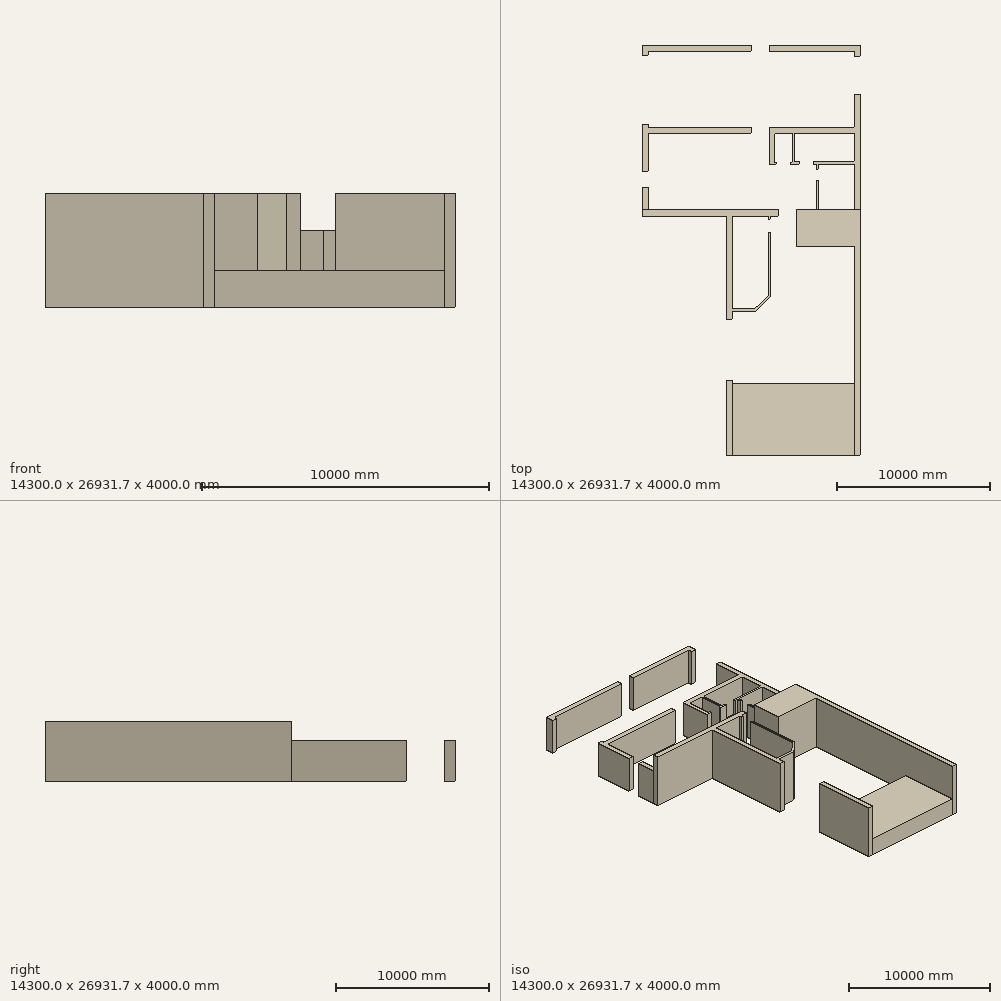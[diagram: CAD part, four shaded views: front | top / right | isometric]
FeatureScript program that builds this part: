
annotation { "Feature Type Name" : "Feature", "Feature Type Description" : "" }
export const myFeature = defineFeature(function(context is Context, id is Id, definition is map)
    precondition{}
    {
        {
            var Q0;
            Q0=qCreatedBy(makeId("Top.planeOp"),FACE);
            var sketch = newSketch(context, id + "F0", { "sketchPlane" : qUnion([Q0])});
            skLineSegment(sketch, "E0.bottom", {"start": v(-6984.38, 2004.34) * mm, "end": v(-234.38, 2004.34) * mm});
            skLineSegment(sketch, "E0.top", {"start": v(-6984.38, -2995.66) * mm, "end": v(-234.38, -2995.66) * mm});
            skLineSegment(sketch, "E0.left", {"start": v(-6984.38, 2004.34) * mm, "end": v(-6984.38, 1751.04) * mm});
            skLineSegment(sketch, "E0.right", {"start": v(6515.62, 2004.34) * mm, "end": v(6515.62, 1701.04) * mm});
            skLineSegment(sketch, "E1.0", {"start": v(-7384.38, 2404.34) * mm, "end": v(-234.38, 2404.34) * mm});
            skLineSegment(sketch, "E1.1", {"start": v(-7384.38, 2404.34) * mm, "end": v(-7384.38, 1751.04) * mm});
            skLineSegment(sketch, "E1.2", {"start": v(-7384.38, -3395.66) * mm, "end": v(-234.38, -3395.66) * mm});
            skLineSegment(sketch, "E1.3", {"start": v(6915.62, 2404.34) * mm, "end": v(6915.62, 1701.04) * mm});
            skLineSegment(sketch, "E2", {"start": v(-234.38, -3395.66) * mm, "end": v(-234.38, -2995.66) * mm});
            skLineSegment(sketch, "E3", {"start": v(965.62, -2995.66) * mm, "end": v(965.62, -3395.66) * mm});
            skLineSegment(sketch, "E4.trimOffspring", {"start": v(965.62, -2995.66) * mm, "end": v(6515.62, -2995.66) * mm});
            skLineSegment(sketch, "E5.trimOffspring", {"start": v(2615.62, -3395.66) * mm, "end": v(6515.62, -3395.66) * mm});
            skLineSegment(sketch, "E6", {"start": v(6515.62, 1701.04) * mm, "end": v(6915.62, 1701.04) * mm});
            skLineSegment(sketch, "E7", {"start": v(6515.62, -798.96) * mm, "end": v(6915.62, -798.96) * mm});
            skLineSegment(sketch, "E8", {"start": v(965.62, 2004.34) * mm, "end": v(965.62, 2404.34) * mm});
            skLineSegment(sketch, "E9", {"start": v(-234.38, 2004.34) * mm, "end": v(-234.38, 2404.34) * mm});
            skPoint(sketch, "E9.endSnap0", {"position": v(-234.38, 2004.34) * mm});
            skLineSegment(sketch, "E10.trimOffspring", {"start": v(965.62, 2404.34) * mm, "end": v(6915.62, 2404.34) * mm});
            skLineSegment(sketch, "E11.trimOffspring", {"start": v(965.62, 2004.34) * mm, "end": v(6515.62, 2004.34) * mm});
            skLineSegment(sketch, "E12.trimOffspring", {"start": v(6515.62, -798.96) * mm, "end": v(6515.62, -2995.66) * mm});
            skLineSegment(sketch, "E13.trimOffspring", {"start": v(6915.62, -798.96) * mm, "end": v(6915.62, -3395.66) * mm});
            skLineSegment(sketch, "E14", {"start": v(-6984.38, 1751.04) * mm, "end": v(-7384.38, 1751.04) * mm});
            skLineSegment(sketch, "E15", {"start": v(-6984.38, -2795.46) * mm, "end": v(-7384.38, -2795.46) * mm});
            skLineSegment(sketch, "E16.trimOffspring", {"start": v(-6984.38, -2795.46) * mm, "end": v(-6984.38, -2995.66) * mm});
            skLineSegment(sketch, "E17.trimOffspring", {"start": v(-7384.38, -2795.46) * mm, "end": v(-7384.38, -3395.66) * mm});
            skLineSegment(sketch, "E18", {"start": v(-7384.38, -3395.66) * mm, "end": v(-7384.38, -5895.66) * mm});
            skLineSegment(sketch, "E19", {"start": v(6915.62, -8795.66) * mm, "end": v(6915.62, -3395.66) * mm});
            skLineSegment(sketch, "E20", {"start": v(6915.62, -8795.66) * mm, "end": v(6915.62, -24527.4) * mm});
            skLineSegment(sketch, "E21", {"start": v(-1884.38, -24527.4) * mm, "end": v(6915.62, -24527.4) * mm});
            skLineSegment(sketch, "E22", {"start": v(-1884.38, -8795.66) * mm, "end": v(-1884.38, -15595.66) * mm});
            skLineSegment(sketch, "E23", {"start": v(965.62, -3395.66) * mm, "end": v(965.62, -5395.66) * mm});
            skLineSegment(sketch, "E24", {"start": v(965.62, -5395.66) * mm, "end": v(1415.62, -5395.66) * mm});
            skLineSegment(sketch, "E25", {"start": v(4015.62, -5395.66) * mm, "end": v(4015.62, -5712.64) * mm});
            skLineSegment(sketch, "E26", {"start": v(6515.62, -3395.66) * mm, "end": v(6515.62, -5245.66) * mm});
            skLineSegment(sketch, "E27", {"start": v(-6984.38, -3395.66) * mm, "end": v(-6984.38, -5895.66) * mm});
            skLineSegment(sketch, "E28", {"start": v(-6984.38, -8395.66) * mm, "end": v(-1484.38, -8395.66) * mm});
            skLineSegment(sketch, "E29", {"start": v(-1484.38, -8795.66) * mm, "end": v(-1484.38, -14889.25) * mm});
            skLineSegment(sketch, "E30", {"start": v(4165.62, -5395.66) * mm, "end": v(6515.62, -5395.66) * mm});
            skLineSegment(sketch, "E31", {"start": v(6515.62, -8395.66) * mm, "end": v(4165.62, -8395.66) * mm});
            skLineSegment(sketch, "E32.trimOffspring", {"start": v(-1884.38, -8795.66) * mm, "end": v(-7384.38, -8795.66) * mm});
            skLineSegment(sketch, "E33.trimOffspring", {"start": v(6515.62, -10827.4) * mm, "end": v(6515.62, -24527.4) * mm});
            skLineSegment(sketch, "E34", {"start": v(2715.62, -8395.66) * mm, "end": v(2715.62, -8795.66) * mm});
            skLineSegment(sketch, "E35", {"start": v(2715.62, -10827.4) * mm, "end": v(2715.62, -8795.66) * mm});
            skLineSegment(sketch, "E36", {"start": v(2715.62, -10827.4) * mm, "end": v(6515.62, -10827.4) * mm});
            skLineSegment(sketch, "E37", {"start": v(-1484.38, -19827.4) * mm, "end": v(6515.62, -19827.4) * mm});
            skLineSegment(sketch, "E38", {"start": v(-1484.38, -8395.66) * mm, "end": v(1515.62, -8395.66) * mm});
            skLineSegment(sketch, "E39", {"start": v(1515.62, -8395.66) * mm, "end": v(1515.62, -8795.66) * mm});
            skLineSegment(sketch, "E40", {"start": v(1515.62, -8795.66) * mm, "end": v(1015.62, -8795.66) * mm});
            skLineSegment(sketch, "E41", {"start": v(1015.62, -8795.66) * mm, "end": v(1015.62, -8995.66) * mm});
            skLineSegment(sketch, "E42", {"start": v(2465.62, -5280.52) * mm, "end": v(2465.62, -3395.66) * mm});
            skLineSegment(sketch, "E43", {"start": v(2615.62, -5245.66) * mm, "end": v(2615.62, -3395.66) * mm});
            skLineSegment(sketch, "E44", {"start": v(1265.62, -5280.52) * mm, "end": v(1265.62, -3410) * mm});
            skLineSegment(sketch, "E45", {"start": v(2465.62, -3395.66) * mm, "end": v(1265.62, -3410) * mm});
            skLineSegment(sketch, "E46", {"start": v(1265.62, -5280.52) * mm, "end": v(1415.62, -5280.52) * mm});
            skLineSegment(sketch, "E47.trimOffspring", {"start": v(6515.62, -5395.66) * mm, "end": v(6515.62, -8395.66) * mm});
            skLineSegment(sketch, "E48", {"start": v(4165.62, -8395.66) * mm, "end": v(4165.62, -6453.64) * mm});
            skLineSegment(sketch, "E49.trimOffspring", {"start": v(4015.62, -8395.66) * mm, "end": v(2715.62, -8395.66) * mm});
            skLineSegment(sketch, "E50", {"start": v(2315.62, -5395.66) * mm, "end": v(2315.62, -5280.52) * mm});
            skLineSegment(sketch, "E51", {"start": v(1415.62, -5395.66) * mm, "end": v(1415.62, -5280.52) * mm});
            skLineSegment(sketch, "E52.trimOffspring", {"start": v(2315.62, -5280.52) * mm, "end": v(2465.62, -5280.52) * mm});
            skLineSegment(sketch, "E53", {"start": v(4015.62, -5712.64) * mm, "end": v(4165.62, -5712.64) * mm});
            skLineSegment(sketch, "E54", {"start": v(4015.62, -6453.64) * mm, "end": v(4165.62, -6453.64) * mm});
            skLineSegment(sketch, "E55.trimOffspring", {"start": v(4165.62, -5712.64) * mm, "end": v(4165.62, -5395.66) * mm});
            skLineSegment(sketch, "E56.trimOffspring", {"start": v(4015.62, -6453.64) * mm, "end": v(4015.62, -8395.66) * mm});
            skLineSegment(sketch, "E57", {"start": v(3815.62, -5395.66) * mm, "end": v(3815.62, -5245.66) * mm});
            skLineSegment(sketch, "E58.trimOffspring", {"start": v(3815.62, -5245.66) * mm, "end": v(6515.62, -5245.66) * mm});
            skLineSegment(sketch, "E59.trimOffspring", {"start": v(3815.62, -5395.66) * mm, "end": v(4015.62, -5395.66) * mm});
            skLineSegment(sketch, "E60", {"start": v(2615.62, -5245.66) * mm, "end": v(2915.62, -5245.66) * mm});
            skLineSegment(sketch, "E61", {"start": v(2315.62, -5395.66) * mm, "end": v(2915.62, -5395.66) * mm});
            skLineSegment(sketch, "E62", {"start": v(2915.62, -5245.66) * mm, "end": v(2915.62, -5395.66) * mm});
            skLineSegment(sketch, "E63", {"start": v(-7384.38, -5895.66) * mm, "end": v(-6984.38, -5895.66) * mm});
            skLineSegment(sketch, "E64", {"start": v(-6984.38, -6895.66) * mm, "end": v(-7384.38, -6895.66) * mm});
            skLineSegment(sketch, "E65.trimOffspring", {"start": v(-6984.38, -6895.66) * mm, "end": v(-6984.38, -8395.66) * mm});
            skLineSegment(sketch, "E66.trimOffspring", {"start": v(-7384.38, -6895.66) * mm, "end": v(-7384.38, -8795.66) * mm});
            skLineSegment(sketch, "E67", {"start": v(1015.62, -14135.65) * mm, "end": v(0, -15095.66) * mm});
            skLineSegment(sketch, "E68", {"start": v(-1484.38, -15095.66) * mm, "end": v(0, -15095.66) * mm});
            skLineSegment(sketch, "E69", {"start": v(865.62, -8795.66) * mm, "end": v(865.62, -8995.66) * mm});
            skLineSegment(sketch, "E70", {"start": v(865.62, -14071.03) * mm, "end": v(0, -14889.25) * mm});
            skLineSegment(sketch, "E71", {"start": v(0, -14889.25) * mm, "end": v(-1484.38, -14889.25) * mm});
            skLineSegment(sketch, "E72", {"start": v(1015.62, -8995.66) * mm, "end": v(865.62, -8995.66) * mm});
            skLineSegment(sketch, "E73", {"start": v(1015.62, -9895.66) * mm, "end": v(865.62, -9895.66) * mm});
            skLineSegment(sketch, "E74.trimOffspring", {"start": v(865.62, -9895.66) * mm, "end": v(865.62, -14071.03) * mm});
            skLineSegment(sketch, "E75.trimOffspring", {"start": v(865.62, -8795.66) * mm, "end": v(-1484.38, -8795.66) * mm});
            skLineSegment(sketch, "E76.trimOffspring", {"start": v(-1484.38, -15095.66) * mm, "end": v(-1484.38, -15595.66) * mm});
            skLineSegment(sketch, "E77", {"start": v(-1484.38, -8795.66) * mm, "end": v(-1884.38, -8795.66) * mm});
            skLineSegment(sketch, "E78", {"start": v(4165.62, -8395.66) * mm, "end": v(4015.62, -8395.66) * mm});
            skLineSegment(sketch, "E79", {"start": v(6515.62, -8395.66) * mm, "end": v(6915.62, -8395.66) * mm});
            skLineSegment(sketch, "E80", {"start": v(-1484.38, -15595.66) * mm, "end": v(-1884.38, -15595.66) * mm});
            skLineSegment(sketch, "E81", {"start": v(-1884.38, -19595.66) * mm, "end": v(-1484.38, -19595.66) * mm});
            skLineSegment(sketch, "E82.trimOffspring", {"start": v(-1484.38, -19595.66) * mm, "end": v(-1484.38, -24527.4) * mm});
            skLineSegment(sketch, "E83.trimOffspring", {"start": v(-1884.38, -19595.66) * mm, "end": v(-1884.38, -24527.4) * mm});
            skLineSegment(sketch, "E84", {"start": v(1015.62, -14135.65) * mm, "end": v(1015.62, -9895.66) * mm});
            skLineSegment(sketch, "E85", {"start": v(-6984.38, -8395.66) * mm, "end": v(-7384.38, -8395.66) * mm});
            skSolve(sketch);
        }
        {
            var Q0;
            Q0=makeQuery(id+"F0.imprint","IMPRINT",FACE,{"disambiguationData":[TD([[makeQuery(id+"F0.imprint","IMPRINT",EDGE,{"derivedFrom":sQuery(id+"F0.wireOp",EDGE,"E0.bottom")}),1.0]])]});
            var Q1;
            Q1=makeQuery(id+"F0.imprint","IMPRINT",FACE,{"disambiguationData":[TD([[makeQuery(id+"F0.imprint","IMPRINT",EDGE,{"derivedFrom":sQuery(id+"F0.wireOp",EDGE,"E0.right")}),1.0]])]});
            var Q2;
            Q2=makeQuery(id+"F0.imprint","IMPRINT",FACE,{"disambiguationData":[TD([[makeQuery(id+"F0.imprint","IMPRINT",EDGE,{"derivedFrom":sQuery(id+"F0.wireOp",EDGE,"E3")}),1.0]])]});
            var Q3;
            {var subQ0=sQuery(id+"F0.wireOp",EDGE,"E18");Q3=makeQuery(id+"F0.imprint","IMPRINT",FACE,{"disambiguationData":[TD([[makeQuery(id+"F0.imprint","IMPRINT",EDGE,{"derivedFrom":subQ0}),1.0]])]});}
            var Q4;
            Q4=makeQuery(id+"F0.imprint","IMPRINT",FACE,{"disambiguationData":[TD([[makeQuery(id+"F0.imprint","IMPRINT",EDGE,{"derivedFrom":sQuery(id+"F0.wireOp",EDGE,"E0.top")}),-1.0]])]});
            var Q5;
            Q5=makeQuery(id+"F0.imprint","IMPRINT",FACE,{"disambiguationData":[TD([[makeQuery(id+"F0.imprint","IMPRINT",EDGE,{"derivedFrom":sQuery(id+"F0.wireOp",EDGE,"E48")}),1.0]])]});
            var Q6;
            {var subQ0=sQuery(id+"F0.wireOp",EDGE,"E64");Q6=makeQuery(id+"F0.imprint","IMPRINT",FACE,{"disambiguationData":[TD([[makeQuery(id+"F0.imprint","IMPRINT",EDGE,{"derivedFrom":subQ0}),1.0]])]});}
            extrude(context, id + "F1", {"entities" : qUnion([Q0, Q1, Q2, Q3, Q4, Q5, Q6]), "depth" : 2700 * mm});
        }
        {
            var Q0;
            {var subQ1=sQuery(id+"F0.wireOp",EDGE,"E22");Q0=makeQuery(id+"F0.imprint","IMPRINT",FACE,{"disambiguationData":[TD([[makeQuery(id+"F0.imprint","IMPRINT",EDGE,{"derivedFrom":subQ1}),1.0]])]});}
            var Q1;
            {var subQ5=sQuery(id+"F0.wireOp",EDGE,"E20");Q1=makeQuery(id+"F0.imprint","IMPRINT",FACE,{"disambiguationData":[TD([[makeQuery(id+"F0.imprint","IMPRINT",EDGE,{"derivedFrom":subQ5}),-1.0]])]});}
            var Q2;
            {var subQ2=sQuery(id+"F0.wireOp",EDGE,"E81");Q2=makeQuery(id+"F0.imprint","IMPRINT",FACE,{"disambiguationData":[TD([[makeQuery(id+"F0.imprint","IMPRINT",EDGE,{"derivedFrom":subQ2}),-1.0]])]});}
            var Q3;
            Q3=makeQuery(id+"F0.imprint","IMPRINT",FACE,{"disambiguationData":[TD([[makeQuery(id+"F0.imprint","IMPRINT",EDGE,{"derivedFrom":sQuery(id+"F0.wireOp",EDGE,"E28")}),-1.0]])]});
            extrude(context, id + "F2", {"entities" : qUnion([Q0, Q1, Q2, Q3]), "depth" : 4000 * mm});
        }
        {
            var Q0;
            {var subQ5=sQuery(id+"F0.wireOp",EDGE,"E37");Q0=makeQuery(id+"F0.imprint","IMPRINT",FACE,{"disambiguationData":[TD([[makeQuery(id+"F0.imprint","IMPRINT",EDGE,{"derivedFrom":subQ5}),-1.0]])]});}
            extrude(context, id + "F3", {"entities" : qUnion([Q0]), "depth" : 1300 * mm});
        }
    });
